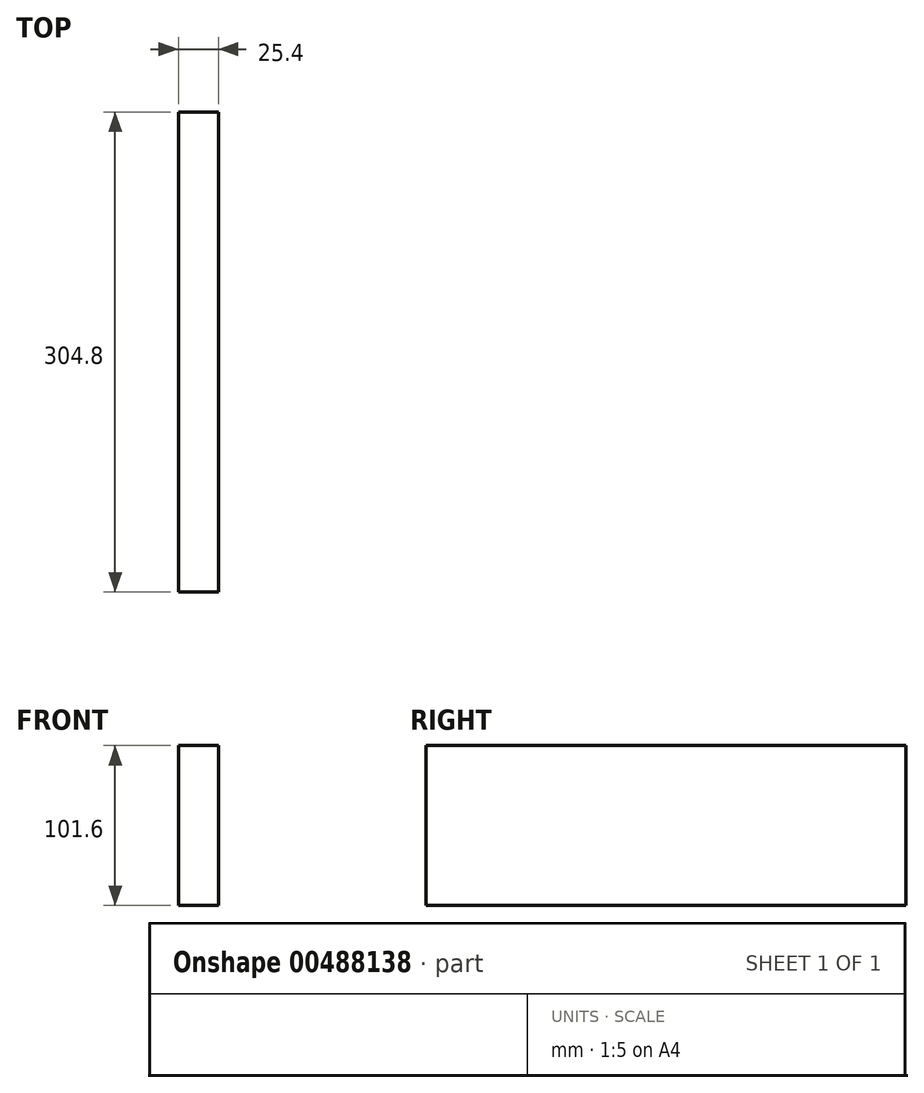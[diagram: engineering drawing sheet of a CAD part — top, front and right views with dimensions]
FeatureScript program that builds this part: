
annotation { "Feature Type Name" : "Feature", "Feature Type Description" : "" }
export const myFeature = defineFeature(function(context is Context, id is Id, definition is map)
    precondition{}
    {
        {
            var Q0;
            Q0=qCreatedBy(makeId("Front.planeOp"),FACE);
            var sketch = newSketch(context, id + "F0", { "sketchPlane" : qUnion([Q0])});
            skLineSegment(sketch, "E0", {"start": v(0, 0) * mm, "end": v(0, 0) * mm});
            skLineSegment(sketch, "E1", {"start": v(0, 0) * mm, "end": v(25.4, 0) * mm});
            skLineSegment(sketch, "E2", {"start": v(25.4, 0) * mm, "end": v(25.4, -101.6) * mm});
            skLineSegment(sketch, "E3", {"start": v(25.4, -101.6) * mm, "end": v(0, -101.6) * mm});
            skLineSegment(sketch, "E4", {"start": v(0, -101.6) * mm, "end": v(0, 0) * mm});
            skSolve(sketch);
        }
        {
            var Q0;
            Q0=makeQuery(id+"F0.imprint","IMPRINT",FACE,{"disambiguationData":[TD([[makeQuery(id+"F0.imprint","IMPRINT",EDGE,{"derivedFrom":sQuery(id+"F0.wireOp",EDGE,"E1")}),-1.0]])]});
            extrude(context, id + "F1", {"entities" : qUnion([Q0]), "depth" : 304.8 * mm, "offsetDistance" : 25.4 * mm});
        }
    });
